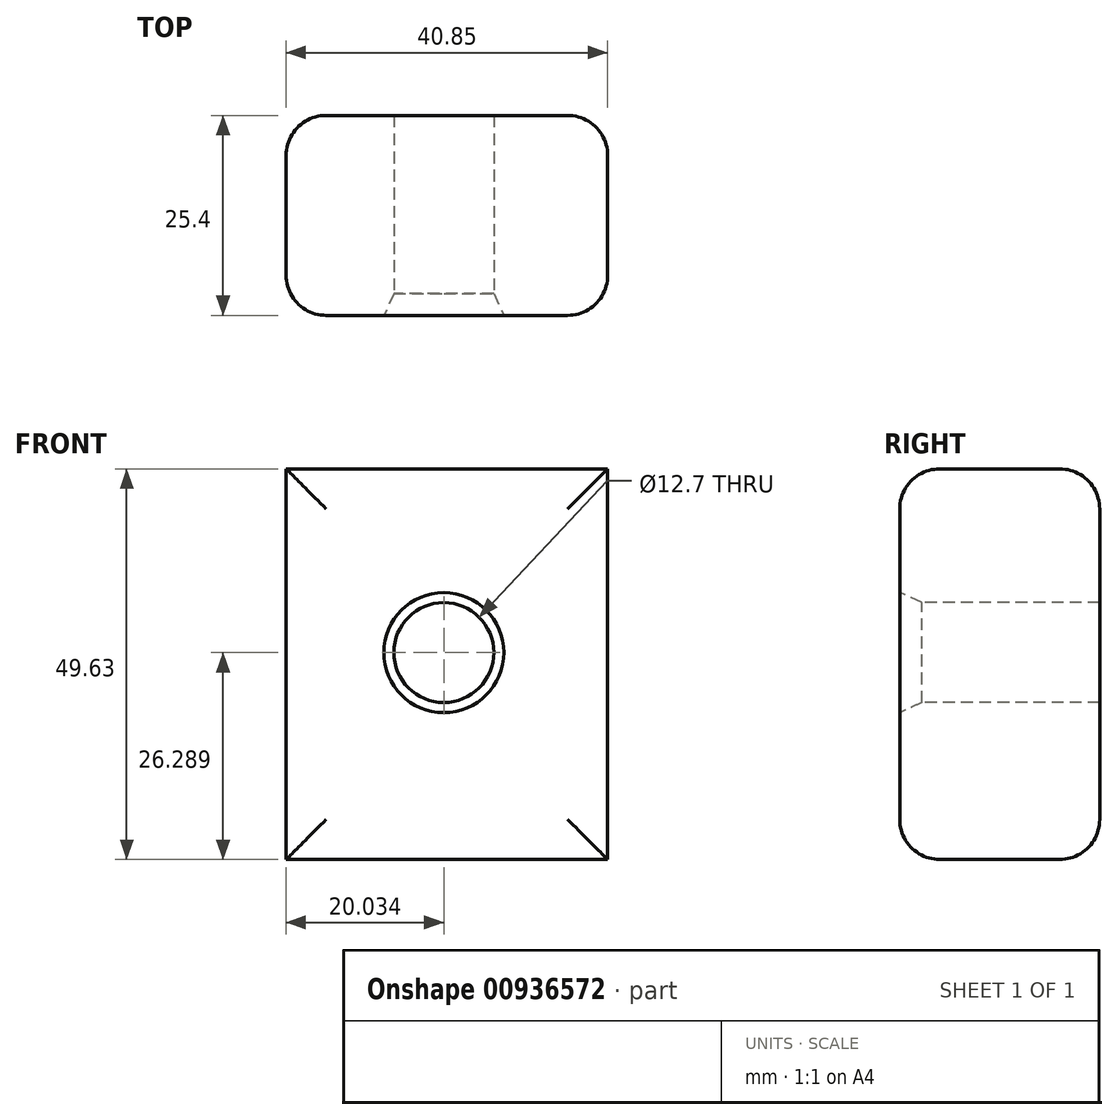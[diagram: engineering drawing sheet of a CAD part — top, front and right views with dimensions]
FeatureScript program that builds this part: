
annotation { "Feature Type Name" : "Feature", "Feature Type Description" : "" }
export const myFeature = defineFeature(function(context is Context, id is Id, definition is map)
    precondition{}
    {
        {
            var Q0;
            Q0=qCreatedBy(makeId("Front.planeOp"),FACE);
            var sketch = newSketch(context, id + "F0", { "sketchPlane" : qUnion([Q0])});
            skLineSegment(sketch, "E0.bottom", {"start": v(-62.43, 37.17) * mm, "end": v(-21.58, 37.17) * mm});
            skLineSegment(sketch, "E0.top", {"start": v(-62.43, -12.46) * mm, "end": v(-21.58, -12.46) * mm});
            skLineSegment(sketch, "E0.left", {"start": v(-62.43, 37.17) * mm, "end": v(-62.43, -12.46) * mm});
            skLineSegment(sketch, "E0.right", {"start": v(-21.58, 37.17) * mm, "end": v(-21.58, -12.46) * mm});
            skSolve(sketch);
        }
        {
            var Q0;
            Q0 = qSketchRegion(id + "F0", true);
            extrude(context, id + "F1", {"entities" : qUnion([Q0]), "depth" : 25.4 * mm, "offsetDistance" : 25.4 * mm});
        }
        {
            var Q0;
            Q0=makeQuery(id+"F1.opExtrude","CAP_FACE",FACE,{"disambiguationData":[OSD([sQuery(id+"F0.wireOp",EDGE,"E0.bottom"),sQuery(id+"F0.wireOp",EDGE,"E0.top"),sQuery(id+"F0.wireOp",EDGE,"E0.left"),sQuery(id+"F0.wireOp",EDGE,"E0.right")])],"isStart":false});
            var Q1;
            Q1=makeQuery(id+"F1.opExtrude","CAP_FACE",FACE,{"disambiguationData":[OSD([sQuery(id+"F0.wireOp",EDGE,"E0.bottom"),sQuery(id+"F0.wireOp",EDGE,"E0.top"),sQuery(id+"F0.wireOp",EDGE,"E0.left"),sQuery(id+"F0.wireOp",EDGE,"E0.right")])],"isStart":true});
            fillet(context, id + "F2", {"entities" : qUnion([Q0, Q1]), "radius" : 5.08 * mm, "tangentPropagation" : true, "allowEdgeOverflow" : false});
        }
        {
            var Q0;
            Q0=makeQuery(id+"F1.opExtrude","CAP_FACE",FACE,{"disambiguationData":[OSD([sQuery(id+"F0.wireOp",EDGE,"E0.bottom"),sQuery(id+"F0.wireOp",EDGE,"E0.top"),sQuery(id+"F0.wireOp",EDGE,"E0.left"),sQuery(id+"F0.wireOp",EDGE,"E0.right")])],"isStart":false});
            var sketch = newSketch(context, id + "F3", { "sketchPlane" : qUnion([Q0])});
            skPoint(sketch, "E1", {"position": v(-42.4, 13.83) * mm});
            skSolve(sketch);
        }
        {
            var Q0;
            Q0=sQuery(id+"F3.wireOp",VERTEX,"E1");
            var Q1;
            Q1=makeQuery(id+"F1.opExtrude","SWEPT_BODY",BODY,{"disambiguationData":[OSD([sQuery(id+"F0.wireOp",EDGE,"E0.bottom"),sQuery(id+"F0.wireOp",EDGE,"E0.top"),sQuery(id+"F0.wireOp",EDGE,"E0.left"),sQuery(id+"F0.wireOp",EDGE,"E0.right")])]});
            hole(context, id + "F4", {"style" : HoleStyle.C_SINK, "endStyle" : HoleEndStyle.THROUGH, "holeDiameter" : 12.7 * mm, "cSinkDiameter" : 15.24 * mm, "cSinkAngle" : 49 * degree, "majorDiameter" : 6.35 * mm, "isTappedThrough" : true, "tappedDepth" : 12.7 * mm, "tapClearance" : 3, "startFromSketch" : true, "locations" : qUnion([Q0]), "scope" : qUnion([Q1])});
        }
    });
